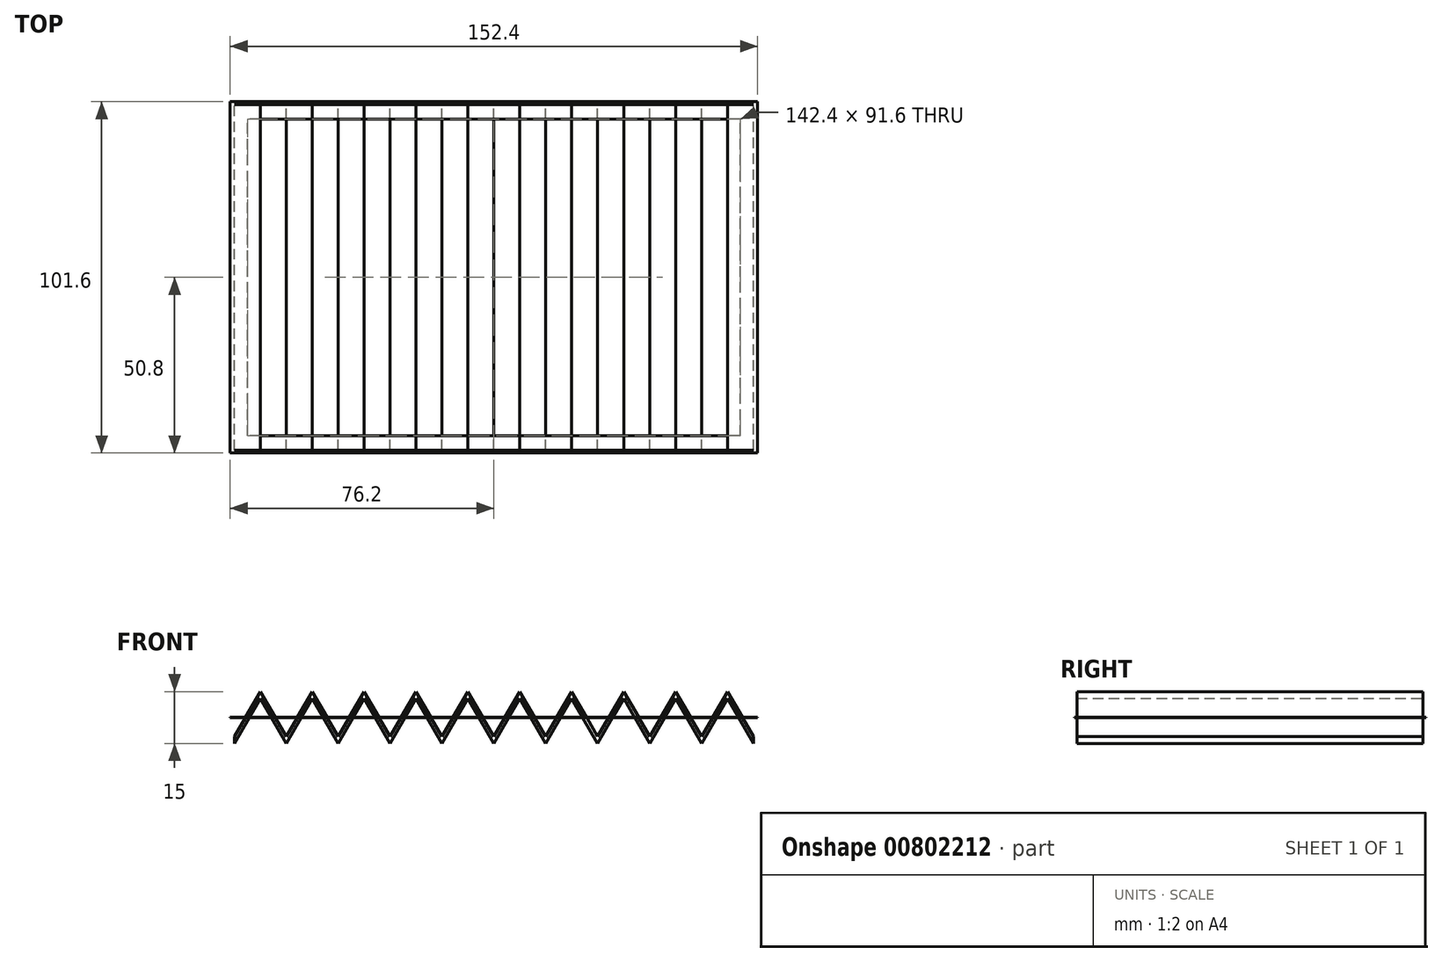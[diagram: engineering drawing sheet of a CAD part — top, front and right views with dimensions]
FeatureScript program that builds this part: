
annotation { "Feature Type Name" : "Feature", "Feature Type Description" : "" }
export const myFeature = defineFeature(function(context is Context, id is Id, definition is map)
    precondition{}
    {
        {
            var Q0;
            Q0=qCreatedBy(makeId("Front.planeOp"),FACE);
            var sketch = newSketch(context, id + "F0", { "sketchPlane" : qUnion([Q0])});
            skLineSegment(sketch, "E0", {"start": v(-75, -5.5) * mm, "end": v(-67.5, 7.5) * mm});
            skLineSegment(sketch, "E1", {"start": v(-67.5, 7.5) * mm, "end": v(-60, -5.5) * mm});
            skLineSegment(sketch, "E2.0", {"start": v(-67.5, 5.5) * mm, "end": v(-60, -7.5) * mm});
            skLineSegment(sketch, "E2.1", {"start": v(-75, -7.5) * mm, "end": v(-67.5, 5.5) * mm});
            skLineSegment(sketch, "E3", {"start": v(-75, -5.5) * mm, "end": v(-75, -7.5) * mm, "construction": true});
            skLineSegment(sketch, "E4", {"start": v(-60, -5.5) * mm, "end": v(-60, -7.5) * mm, "construction": true});
            skLineSegment(sketch, "E5", {"start": v(-75, -7.5) * mm, "end": v(-67.5, -7.5) * mm, "construction": true});
            skLineSegment(sketch, "E6", {"start": v(-67.5, -7.5) * mm, "end": v(-60, -7.5) * mm, "construction": true});
            skLineSegment(sketch, "E7", {"start": v(-75, -5.5) * mm, "end": v(75, -5.5) * mm, "construction": true});
            skLineSegment(sketch, "E8.1.0.0", {"start": v(-60, -5.5) * mm, "end": v(-52.5, 7.5) * mm});
            skLineSegment(sketch, "E8.1.0.1", {"start": v(-60, -7.5) * mm, "end": v(-52.5, 5.5) * mm});
            skLineSegment(sketch, "E8.1.0.2", {"start": v(-52.5, 5.5) * mm, "end": v(-45, -7.5) * mm});
            skLineSegment(sketch, "E8.1.0.3", {"start": v(-52.5, 7.5) * mm, "end": v(-45, -5.5) * mm});
            skLineSegment(sketch, "E8.2.0.0", {"start": v(-45, -5.5) * mm, "end": v(-37.5, 7.5) * mm});
            skLineSegment(sketch, "E8.2.0.1", {"start": v(-45, -7.5) * mm, "end": v(-37.5, 5.5) * mm});
            skLineSegment(sketch, "E8.2.0.2", {"start": v(-37.5, 5.5) * mm, "end": v(-30, -7.5) * mm});
            skLineSegment(sketch, "E8.2.0.3", {"start": v(-37.5, 7.5) * mm, "end": v(-30, -5.5) * mm});
            skLineSegment(sketch, "E8.direction1", {"start": v(-75, -5.5) * mm, "end": v(-60, -5.5) * mm, "construction": true});
            skLineSegment(sketch, "E9.0.3.0", {"start": v(-30, -5.5) * mm, "end": v(-22.5, 7.5) * mm});
            skLineSegment(sketch, "E9.3.3.0", {"start": v(-30, -7.5) * mm, "end": v(-22.5, 5.5) * mm});
            skLineSegment(sketch, "E9.6.3.0", {"start": v(-22.5, 5.5) * mm, "end": v(-15, -7.5) * mm});
            skLineSegment(sketch, "E9.9.3.0", {"start": v(-22.5, 7.5) * mm, "end": v(-15, -5.5) * mm});
            skLineSegment(sketch, "E9.0.4.0", {"start": v(-15, -5.5) * mm, "end": v(-7.5, 7.5) * mm});
            skLineSegment(sketch, "E9.3.4.0", {"start": v(-15, -7.5) * mm, "end": v(-7.5, 5.5) * mm});
            skLineSegment(sketch, "E9.6.4.0", {"start": v(-7.5, 5.5) * mm, "end": v(0, -7.5) * mm});
            skLineSegment(sketch, "E9.9.4.0", {"start": v(-7.5, 7.5) * mm, "end": v(0, -5.5) * mm});
            skLineSegment(sketch, "E9.0.5.0", {"start": v(0, -5.5) * mm, "end": v(7.5, 7.5) * mm});
            skLineSegment(sketch, "E9.3.5.0", {"start": v(0, -7.5) * mm, "end": v(7.5, 5.5) * mm});
            skLineSegment(sketch, "E9.6.5.0", {"start": v(7.5, 5.5) * mm, "end": v(15, -7.5) * mm});
            skLineSegment(sketch, "E9.9.5.0", {"start": v(7.5, 7.5) * mm, "end": v(15, -5.5) * mm});
            skLineSegment(sketch, "E9.0.6.0", {"start": v(15, -5.5) * mm, "end": v(22.5, 7.5) * mm});
            skLineSegment(sketch, "E9.3.6.0", {"start": v(15, -7.5) * mm, "end": v(22.5, 5.5) * mm});
            skLineSegment(sketch, "E9.6.6.0", {"start": v(22.5, 5.5) * mm, "end": v(30, -7.5) * mm});
            skLineSegment(sketch, "E9.9.6.0", {"start": v(22.5, 7.5) * mm, "end": v(30, -5.5) * mm});
            skLineSegment(sketch, "E9.0.7.0", {"start": v(30, -5.5) * mm, "end": v(37.5, 7.5) * mm});
            skLineSegment(sketch, "E9.3.7.0", {"start": v(30, -7.5) * mm, "end": v(37.5, 5.5) * mm});
            skLineSegment(sketch, "E9.6.7.0", {"start": v(37.5, 5.5) * mm, "end": v(45, -7.5) * mm});
            skLineSegment(sketch, "E9.9.7.0", {"start": v(37.5, 7.5) * mm, "end": v(45, -5.5) * mm});
            skLineSegment(sketch, "E9.0.8.0", {"start": v(45, -5.5) * mm, "end": v(52.5, 7.5) * mm});
            skLineSegment(sketch, "E9.3.8.0", {"start": v(45, -7.5) * mm, "end": v(52.5, 5.5) * mm});
            skLineSegment(sketch, "E9.6.8.0", {"start": v(52.5, 5.5) * mm, "end": v(60, -7.5) * mm});
            skLineSegment(sketch, "E9.9.8.0", {"start": v(52.5, 7.5) * mm, "end": v(60, -5.5) * mm});
            skLineSegment(sketch, "E9.0.9.0", {"start": v(60, -5.5) * mm, "end": v(67.5, 7.5) * mm});
            skLineSegment(sketch, "E9.3.9.0", {"start": v(60, -7.5) * mm, "end": v(67.5, 5.5) * mm});
            skLineSegment(sketch, "E9.6.9.0", {"start": v(67.5, 5.5) * mm, "end": v(75, -7.5) * mm});
            skLineSegment(sketch, "E9.9.9.0", {"start": v(67.5, 7.5) * mm, "end": v(75, -5.5) * mm});
            skLineSegment(sketch, "E10", {"start": v(-75, -5.5) * mm, "end": v(-75, -7.5) * mm});
            skLineSegment(sketch, "E11", {"start": v(75, -5.5) * mm, "end": v(75, -7.5) * mm});
            skLineSegment(sketch, "E12", {"start": v(0, -7.5) * mm, "end": v(0, 0) * mm, "construction": true});
            skSolve(sketch);
        }
        {
            var Q0;
            Q0=makeQuery(id+"F0.imprint","IMPRINT",FACE,{"disambiguationData":[TD([[makeQuery(id+"F0.imprint","IMPRINT",EDGE,{"derivedFrom":sQuery(id+"F0.wireOp",EDGE,"E0")}),-1.0]])]});
            var Q1;
            Q1=makeQuery(id+"F0.imprint","IMPRINT",FACE,{"disambiguationData":[TD([[makeQuery(id+"F0.imprint","IMPRINT",EDGE,{"derivedFrom":sQuery(id+"F0.wireOp",EDGE,"4c44e779-d75e-411a-95ac-4b086d79ddcc.1.0.0")}),-1.0]])]});
            var Q2;
            Q2=makeQuery(id+"F0.imprint","IMPRINT",FACE,{"disambiguationData":[TD([[makeQuery(id+"F0.imprint","IMPRINT",EDGE,{"derivedFrom":sQuery(id+"F0.wireOp",EDGE,"4c44e779-d75e-411a-95ac-4b086d79ddcc.2.0.0")}),-1.0]])]});
            var Q3;
            Q3=makeQuery(id+"F0.imprint","IMPRINT",FACE,{"disambiguationData":[TD([[makeQuery(id+"F0.imprint","IMPRINT",EDGE,{"derivedFrom":sQuery(id+"F0.wireOp",EDGE,"bf426145-180c-4fe0-bbf0-b5b7b15b0060.0.3.0")}),-1.0]])]});
            var Q4;
            Q4=makeQuery(id+"F0.imprint","IMPRINT",FACE,{"disambiguationData":[TD([[makeQuery(id+"F0.imprint","IMPRINT",EDGE,{"derivedFrom":sQuery(id+"F0.wireOp",EDGE,"bf426145-180c-4fe0-bbf0-b5b7b15b0060.0.4.0")}),-1.0]])]});
            var Q5;
            Q5=makeQuery(id+"F0.imprint","IMPRINT",FACE,{"disambiguationData":[TD([[makeQuery(id+"F0.imprint","IMPRINT",EDGE,{"derivedFrom":sQuery(id+"F0.wireOp",EDGE,"bf426145-180c-4fe0-bbf0-b5b7b15b0060.0.5.0")}),-1.0]])]});
            var Q6;
            Q6=makeQuery(id+"F0.imprint","IMPRINT",FACE,{"disambiguationData":[TD([[makeQuery(id+"F0.imprint","IMPRINT",EDGE,{"derivedFrom":sQuery(id+"F0.wireOp",EDGE,"bf426145-180c-4fe0-bbf0-b5b7b15b0060.0.6.0")}),-1.0]])]});
            var Q7;
            Q7=makeQuery(id+"F0.imprint","IMPRINT",FACE,{"disambiguationData":[TD([[makeQuery(id+"F0.imprint","IMPRINT",EDGE,{"derivedFrom":sQuery(id+"F0.wireOp",EDGE,"bf426145-180c-4fe0-bbf0-b5b7b15b0060.0.7.0")}),-1.0]])]});
            var Q8;
            Q8=makeQuery(id+"F0.imprint","IMPRINT",FACE,{"disambiguationData":[TD([[makeQuery(id+"F0.imprint","IMPRINT",EDGE,{"derivedFrom":sQuery(id+"F0.wireOp",EDGE,"bf426145-180c-4fe0-bbf0-b5b7b15b0060.0.8.0")}),-1.0]])]});
            var Q9;
            Q9=makeQuery(id+"F0.imprint","IMPRINT",FACE,{"disambiguationData":[TD([[makeQuery(id+"F0.imprint","IMPRINT",EDGE,{"derivedFrom":sQuery(id+"F0.wireOp",EDGE,"bf426145-180c-4fe0-bbf0-b5b7b15b0060.0.9.0")}),-1.0]])]});
            extrude(context, id + "F1", {"entities" : qUnion([Q0, Q1, Q2, Q3, Q4, Q5, Q6, Q7, Q8, Q9]), "endBound" : BoundingType.SYMMETRIC, "depth" : 100 * mm, "offsetDistance" : 25 * mm});
        }
        {
            var Q0;
            Q0=qCreatedBy(makeId("Top.planeOp"),FACE);
            var sketch = newSketch(context, id + "F2", { "sketchPlane" : qUnion([Q0])});
            skLineSegment(sketch, "E13.bottom", {"start": v(76.2, -50.8) * mm, "end": v(-76.2, -50.8) * mm});
            skLineSegment(sketch, "E13.top", {"start": v(76.2, 50.8) * mm, "end": v(-76.2, 50.8) * mm});
            skLineSegment(sketch, "E13.left", {"start": v(76.2, -50.8) * mm, "end": v(76.2, 50.8) * mm});
            skLineSegment(sketch, "E13.right", {"start": v(-76.2, -50.8) * mm, "end": v(-76.2, 50.8) * mm});
            skPoint(sketch, "E13.middle", {"position": v(0, 0) * mm});
            skLineSegment(sketch, "E14.0", {"start": v(71.2, 45.8) * mm, "end": v(-71.2, 45.8) * mm});
            skLineSegment(sketch, "E14.1", {"start": v(71.2, -45.8) * mm, "end": v(71.2, 45.8) * mm});
            skLineSegment(sketch, "E14.2", {"start": v(71.2, -45.8) * mm, "end": v(-71.2, -45.8) * mm});
            skLineSegment(sketch, "E14.3", {"start": v(-71.2, -45.8) * mm, "end": v(-71.2, 45.8) * mm});
            skSolve(sketch);
        }
        {
            var Q0;
            Q0 = qSketchRegion(id + "F2", true);
            extrude(context, id + "F3", {"entities" : qUnion([Q0]), "endBound" : BoundingType.SYMMETRIC, "depth" : 5 / 203.2 * mm, "offsetDistance" : 25 * mm});
        }
    });
